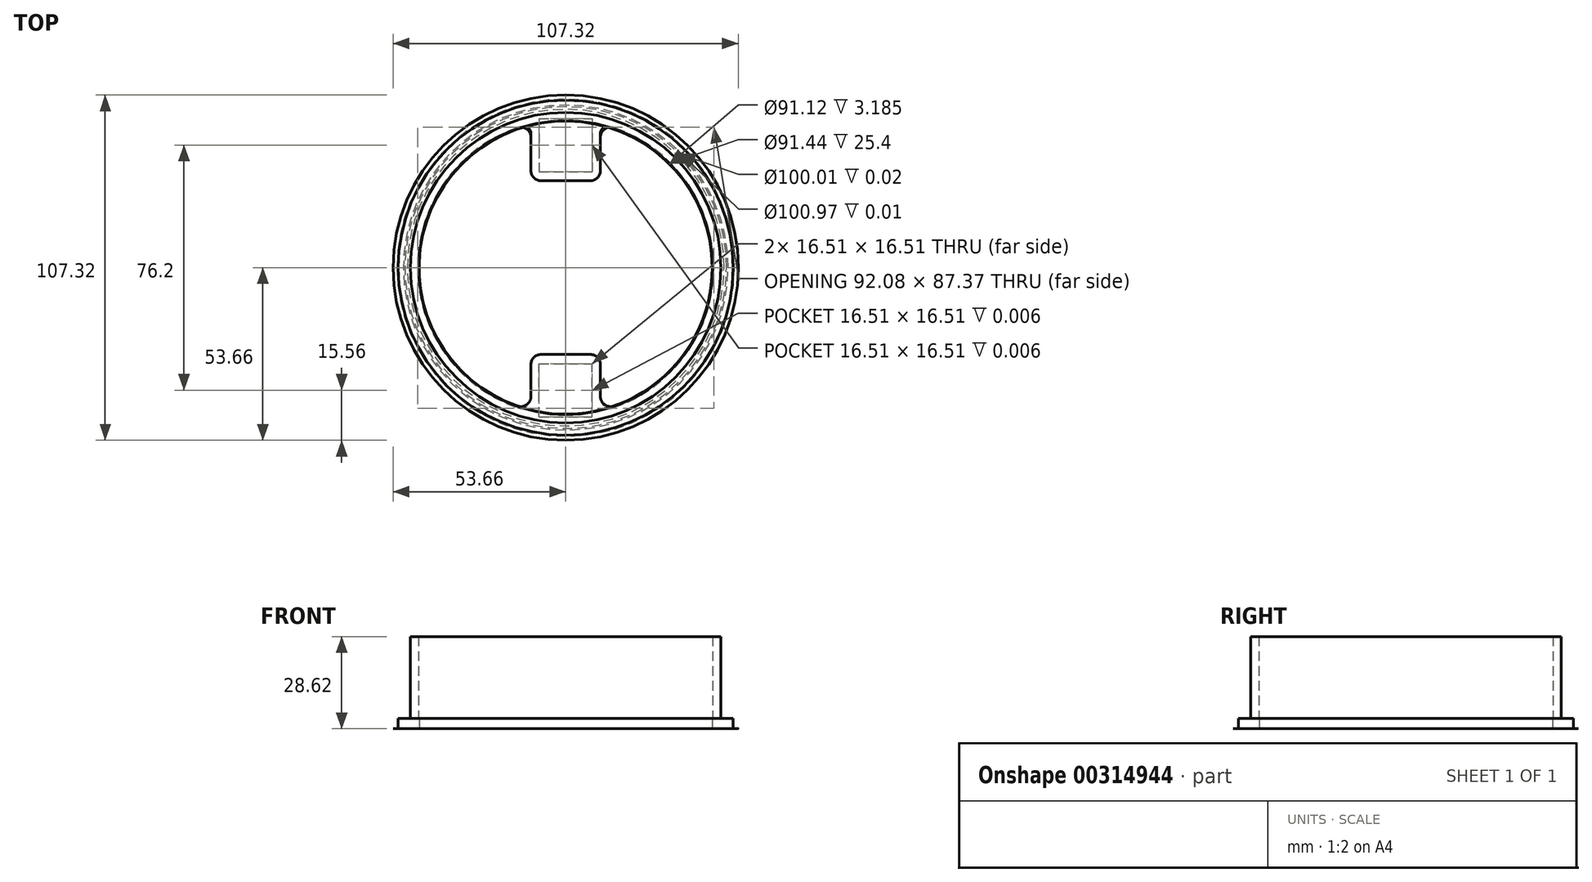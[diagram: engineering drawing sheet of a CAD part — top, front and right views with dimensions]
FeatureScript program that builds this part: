
annotation { "Feature Type Name" : "Feature", "Feature Type Description" : "" }
export const myFeature = defineFeature(function(context is Context, id is Id, definition is map)
    precondition{}
    {
        {
            var Q0;
            Q0=qCreatedBy(makeId("Top.planeOp"),FACE);
            var sketch = newSketch(context, id + "F0", { "sketchPlane" : qUnion([Q0])});
            skCircle(sketch, "E0", {"center": v(0, 0) * mm, "radius": 50 * mm});
            skCircle(sketch, "E1", {"center": v(0, 0) * mm, "radius": 52.39 * mm});
            skSolve(sketch);
        }
        {
            var Q0;
            Q0=qSketchRegion(id+"F0",true);
            extrude(context, id + "F1", {"entities" : qUnion([Q0]), "depth" : 1 / 50.8 * mm});
        }
        {
            var Q0;
            Q0=makeQuery(id+"F1.opExtrude","CAP_FACE",FACE,{"disambiguationData":[OSD([sQuery(id+"F0.wireOp",EDGE,"E0"),sQuery(id+"F0.wireOp",EDGE,"E1")])],"isStart":false});
            var sketch = newSketch(context, id + "F2", { "sketchPlane" : qUnion([Q0])});
            skCircle(sketch, "E2.0", {"center": v(0, 0) * mm, "radius": 52.39 * mm});
            skArc(sketch, "E3.0", {"start": v(-15, 43.52) * mm, "mid": v(-46.04, 0) * mm, "end": v(-15, -43.52) * mm});
            skPoint(sketch, "E4.middle", {"position": v(0, 39.69) * mm});
            skPoint(sketch, "E5.orphan", {"position": v(-12.07, 48.74) * mm});
            skPoint(sketch, "E6.orphan", {"position": v(10.8, 48.25) * mm});
            skLineSegment(sketch, "E7.MirrorCS", {"start": v(-10.8, -40.52) * mm, "end": v(-10.8, -30.16) * mm});
            skArc(sketch, "E8.trimOffspring", {"start": v(15, -43.52) * mm, "mid": v(46.04, 0) * mm, "end": v(15, 43.52) * mm});
            skPoint(sketch, "E9.visualSharp", {"position": v(-10.8, -44.75) * mm});
            skArc(sketch, "E9.filletArc", {"start": v(-15, -43.52) * mm, "mid": v(-12.13, -43.1) * mm, "end": v(-10.8, -40.52) * mm});
            skPoint(sketch, "E10.visualSharp", {"position": v(-10.8, -31.13) * mm});
            skPoint(sketch, "E11.visualSharp", {"position": v(12.06, -32.23) * mm});
            skPoint(sketch, "E12.visualSharp", {"position": v(19.77, -41.58) * mm});
            skPoint(sketch, "E13.visualSharp", {"position": v(-10.8, 31.13) * mm});
            skPoint(sketch, "E14.visualSharp", {"position": v(-10.8, 44.75) * mm});
            skPoint(sketch, "E15.visualSharp", {"position": v(19.77, 41.58) * mm});
            skLineSegment(sketch, "E16", {"start": v(7.62, -26.99) * mm, "end": v(-7.62, -26.99) * mm});
            skPoint(sketch, "E17.visualSharp", {"position": v(7.88, -26.99) * mm});
            skPoint(sketch, "E18.visualSharp", {"position": v(-10.8, -26.99) * mm});
            skArc(sketch, "E18.filletArc", {"start": v(-7.62, -26.99) * mm, "mid": v(-9.87, -27.92) * mm, "end": v(-10.8, -30.16) * mm});
            skLineSegment(sketch, "E19.MirrorCS", {"start": v(7.62, 26.99) * mm, "end": v(-7.62, 26.99) * mm});
            skArc(sketch, "E20.MirrorCS", {"start": v(-7.62, 26.99) * mm, "mid": v(-9.87, 27.92) * mm, "end": v(-10.8, 30.16) * mm});
            skLineSegment(sketch, "E21.MirrorCS", {"start": v(-10.8, 40.52) * mm, "end": v(-10.8, 30.16) * mm});
            skLineSegment(sketch, "E22.MirrorCS", {"start": v(10.8, 40.52) * mm, "end": v(10.8, 30.16) * mm});
            skArc(sketch, "E23.MirrorCS", {"start": v(7.62, 26.99) * mm, "mid": v(9.87, 27.92) * mm, "end": v(10.8, 30.16) * mm});
            skArc(sketch, "E24.MirrorCS", {"start": v(7.62, -26.99) * mm, "mid": v(9.87, -27.92) * mm, "end": v(10.8, -30.16) * mm});
            skLineSegment(sketch, "E25.MirrorCS", {"start": v(10.8, -40.52) * mm, "end": v(10.8, -30.16) * mm});
            skArc(sketch, "E26.MirrorCS", {"start": v(15, -43.52) * mm, "mid": v(12.13, -43.1) * mm, "end": v(10.8, -40.52) * mm});
            skPoint(sketch, "E27.orphan", {"position": v(5.08, 26.99) * mm});
            skPoint(sketch, "E28.orphan", {"position": v(5.08, -26.99) * mm});
            skArc(sketch, "E29.MirrorCS", {"start": v(-15, 43.52) * mm, "mid": v(-12.13, 43.1) * mm, "end": v(-10.8, 40.52) * mm});
            skArc(sketch, "E30.MirrorCS", {"start": v(15, 43.52) * mm, "mid": v(12.13, 43.1) * mm, "end": v(10.8, 40.52) * mm});
            skSolve(sketch);
        }
        {
            var Q0;
            Q0=qSketchRegion(id+"F2",true);
            extrude(context, id + "F3", {"entities" : qUnion([Q0]), "operationType" : NewBodyOperationType.ADD, "depth" : 1 / 101.6 * mm});
        }
        {
            var Q0;
            Q0=makeQuery(id+"F3.opExtrude","CAP_FACE",FACE,{"disambiguationData":[OSD([sQuery(id+"F2.wireOp",EDGE,"E2.0"),sQuery(id+"F2.wireOp",EDGE,"E3.0")])],"isStart":false});
            var sketch = newSketch(context, id + "F4", { "sketchPlane" : qUnion([Q0])});
            skCircle(sketch, "E31", {"center": v(0, 0) * mm, "radius": 50.48 * mm});
            skCircle(sketch, "E32.0", {"center": v(0, 0) * mm, "radius": 53.66 * mm});
            skSolve(sketch);
        }
        {
            var Q0;
            Q0=qSketchRegion(id+"F4",true);
            extrude(context, id + "F5", {"entities" : qUnion([Q0]), "operationType" : NewBodyOperationType.ADD, "depth" : 1 / 101.6 * mm});
        }
        {
            var Q0;
            Q0=makeQuery(id+"F3.opExtrude","CAP_FACE",FACE,{"disambiguationData":[OSD([sQuery(id+"F2.wireOp",EDGE,"E2.0"),sQuery(id+"F2.wireOp",EDGE,"E3.0"),sQuery(id+"F2.wireOp",EDGE,"E4.top"),sQuery(id+"F2.wireOp",EDGE,"E4.left"),sQuery(id+"F2.wireOp",EDGE,"E4.right"),sQuery(id+"F2.wireOp",EDGE,"E7.MirrorCS"),sQuery(id+"F2.wireOp",EDGE,"14d7e438-5bb9-4d8e-acd8-ebce0bf1a9fc0.MirrorCS"),sQuery(id+"F2.wireOp",EDGE,"57ccc243-d271-415f-816b-320263d1c3790.MirrorCS"),sQuery(id+"F2.wireOp",EDGE,"E8.trimOffspring"),sQuery(id+"F2.wireOp",EDGE,"E9.filletArc"),sQuery(id+"F2.wireOp",EDGE,"E10.filletArc"),sQuery(id+"F2.wireOp",EDGE,"E11.filletArc"),sQuery(id+"F2.wireOp",EDGE,"E12.filletArc"),sQuery(id+"F2.wireOp",EDGE,"E13.filletArc"),sQuery(id+"F2.wireOp",EDGE,"E14.filletArc"),sQuery(id+"F2.wireOp",EDGE,"E15.filletArc"),sQuery(id+"F2.wireOp",EDGE,"87325a1d-47ca-4d5e-9cd2-0e4b37ab90e0.filletArc")])],"isStart":false});
            var sketch = newSketch(context, id + "F6", { "sketchPlane" : qUnion([Q0])});
            skLineSegment(sketch, "E33.bottom", {"start": v(8.25, 46.35) * mm, "end": v(-8.26, 46.35) * mm});
            skLineSegment(sketch, "E33.top", {"start": v(8.25, 29.84) * mm, "end": v(-8.26, 29.84) * mm});
            skLineSegment(sketch, "E33.left", {"start": v(8.25, 46.35) * mm, "end": v(8.25, 29.84) * mm});
            skLineSegment(sketch, "E33.right", {"start": v(-8.26, 46.35) * mm, "end": v(-8.26, 29.84) * mm});
            skPoint(sketch, "E33.middle", {"position": v(0, 38.1) * mm});
            skLineSegment(sketch, "E34.MirrorCS", {"start": v(-8.26, -46.35) * mm, "end": v(-8.26, -29.84) * mm});
            skLineSegment(sketch, "E35.MirrorCS", {"start": v(8.25, -46.35) * mm, "end": v(8.25, -29.84) * mm});
            skLineSegment(sketch, "E36.MirrorCS", {"start": v(8.25, -29.84) * mm, "end": v(-8.26, -29.84) * mm});
            skLineSegment(sketch, "E37.MirrorCS", {"start": v(8.25, -46.35) * mm, "end": v(-8.26, -46.35) * mm});
            skPoint(sketch, "E38.MirrorP", {"position": v(0, -38.1) * mm});
            skSolve(sketch);
        }
        {
            var Q0;
            Q0=qSketchRegion(id+"F6",true);
            extrude(context, id + "F7", {"entities" : qUnion([Q0]), "operationType" : NewBodyOperationType.REMOVE, "oppositeDirection" : true, "depth" : 1 / 152.4 * mm});
        }
        {
            var Q0;
            Q0=makeQuery(id+"F5.opExtrude","CAP_FACE",FACE,{"disambiguationData":[OSD([sQuery(id+"F4.wireOp",EDGE,"E31"),sQuery(id+"F4.wireOp",EDGE,"E32.0")])],"isStart":false});
            var sketch = newSketch(context, id + "F8", { "sketchPlane" : qUnion([Q0])});
            skCircle(sketch, "E39.0", {"center": v(0, 0) * mm, "radius": 49.21 * mm});
            skArc(sketch, "E40.0", {"start": v(-10.8, 41.77) * mm, "mid": v(-11.57, 43.3) * mm, "end": v(-13.25, 43.6) * mm});
            skLineSegment(sketch, "E40.7", {"start": v(-10.8, -40.02) * mm, "end": v(-10.8, -30.16) * mm});
            skLineSegment(sketch, "E40.10", {"start": v(10.8, -40.02) * mm, "end": v(10.8, -30.16) * mm});
            skArc(sketch, "E40.13", {"start": v(13.25, 43.6) * mm, "mid": v(11.57, 43.3) * mm, "end": v(10.8, 41.77) * mm});
            skLineSegment(sketch, "E41", {"start": v(-7.62, -26.99) * mm, "end": v(7.62, -26.99) * mm});
            skLineSegment(sketch, "E42.MirrorCS", {"start": v(-7.62, 26.99) * mm, "end": v(7.62, 26.99) * mm});
            skLineSegment(sketch, "E43.MirrorCS", {"start": v(-10.8, 41.77) * mm, "end": v(-10.8, 30.16) * mm});
            skLineSegment(sketch, "E44.MirrorCS", {"start": v(10.8, 41.77) * mm, "end": v(10.8, 30.16) * mm});
            skPoint(sketch, "E45.visualSharp", {"position": v(-10.8, -26.99) * mm});
            skArc(sketch, "E45.filletArc", {"start": v(-7.62, -26.99) * mm, "mid": v(-9.87, -27.92) * mm, "end": v(-10.8, -30.16) * mm});
            skPoint(sketch, "E46.visualSharp", {"position": v(10.8, -26.99) * mm});
            skArc(sketch, "E46.filletArc", {"start": v(10.8, -30.16) * mm, "mid": v(9.87, -27.92) * mm, "end": v(7.62, -26.99) * mm});
            skPoint(sketch, "E47.visualSharp", {"position": v(10.8, 26.99) * mm});
            skArc(sketch, "E47.filletArc", {"start": v(7.62, 26.99) * mm, "mid": v(9.87, 27.92) * mm, "end": v(10.8, 30.16) * mm});
            skPoint(sketch, "E48.visualSharp", {"position": v(-10.8, 26.99) * mm});
            skArc(sketch, "E48.filletArc", {"start": v(-10.8, 30.16) * mm, "mid": v(-9.87, 27.92) * mm, "end": v(-7.62, 26.99) * mm});
            skArc(sketch, "E49", {"start": v(-13.25, 43.6) * mm, "mid": v(-45.55, 0.93) * mm, "end": v(-15.02, -43.02) * mm});
            skPoint(sketch, "E50.orphan", {"position": v(-10.8, -41.36) * mm});
            skPoint(sketch, "E51.orphan", {"position": v(10.8, -41.77) * mm});
            skArc(sketch, "E52.trimOffspring", {"start": v(15.02, -43.02) * mm, "mid": v(45.55, 0.93) * mm, "end": v(13.25, 43.6) * mm});
            skPoint(sketch, "E53.visualSharp", {"position": v(-10.8, -44.26) * mm});
            skArc(sketch, "E53.filletArc", {"start": v(-15.02, -43.02) * mm, "mid": v(-12.13, -42.6) * mm, "end": v(-10.8, -40.02) * mm});
            skPoint(sketch, "E54.visualSharp", {"position": v(10.8, -44.26) * mm});
            skArc(sketch, "E54.filletArc", {"start": v(10.8, -40.02) * mm, "mid": v(12.13, -42.6) * mm, "end": v(15.02, -43.02) * mm});
            skPoint(sketch, "E55.orphan", {"position": v(-10.8, 41.36) * mm});
            skSolve(sketch);
        }
        {
            var Q0;
            Q0=qSketchRegion(id+"F8",true);
            extrude(context, id + "F9", {"entities" : qUnion([Q0]), "operationType" : NewBodyOperationType.ADD, "depth" : 1 / 101.6 * mm});
        }
        {
            var Q0;
            Q0=makeQuery(id+"F9.opExtrude","CAP_FACE",FACE,{"disambiguationData":[OSD([sQuery(id+"F8.wireOp",EDGE,"E39.0"),sQuery(id+"F8.wireOp",EDGE,"E40.0"),sQuery(id+"F8.wireOp",EDGE,"E40.1"),sQuery(id+"F8.wireOp",EDGE,"E40.2"),sQuery(id+"F8.wireOp",EDGE,"E40.3"),sQuery(id+"F8.wireOp",EDGE,"E40.4"),sQuery(id+"F8.wireOp",EDGE,"E40.5"),sQuery(id+"F8.wireOp",EDGE,"E40.6"),sQuery(id+"F8.wireOp",EDGE,"E40.7"),sQuery(id+"F8.wireOp",EDGE,"E40.8"),sQuery(id+"F8.wireOp",EDGE,"E40.9"),sQuery(id+"F8.wireOp",EDGE,"E40.10"),sQuery(id+"F8.wireOp",EDGE,"E40.11"),sQuery(id+"F8.wireOp",EDGE,"E40.12"),sQuery(id+"F8.wireOp",EDGE,"E40.13"),sQuery(id+"F8.wireOp",EDGE,"E40.14"),sQuery(id+"F8.wireOp",EDGE,"E40.15")])],"isStart":false});
            var sketch = newSketch(context, id + "F10", { "sketchPlane" : qUnion([Q0])});
            skCircle(sketch, "E56", {"center": v(0, 0) * mm, "radius": 52.07 * mm});
            skCircle(sketch, "E57", {"center": v(0, 0) * mm, "radius": 45.56 * mm});
            skSolve(sketch);
        }
        {
            var Q0;
            Q0=qSketchRegion(id+"F10",true);
            extrude(context, id + "F11", {"entities" : qUnion([Q0]), "operationType" : NewBodyOperationType.ADD, "depth" : 3.17 * mm});
        }
        {
            var Q0;
            Q0=makeQuery(id+"F11.opExtrude","CAP_FACE",FACE,{"disambiguationData":[OSD([sQuery(id+"F10.wireOp",EDGE,"E56"),sQuery(id+"F10.wireOp",EDGE,"E57")])],"isStart":false});
            var sketch = newSketch(context, id + "F12", { "sketchPlane" : qUnion([Q0])});
            skCircle(sketch, "E58", {"center": v(0, 0) * mm, "radius": 48.26 * mm});
            skCircle(sketch, "E59", {"center": v(0, 0) * mm, "radius": 45.72 * mm});
            skSolve(sketch);
        }
        {
            var Q0;
            Q0=qSketchRegion(id+"F12",true);
            extrude(context, id + "F13", {"entities" : qUnion([Q0]), "operationType" : NewBodyOperationType.ADD, "depth" : 25.4 * mm});
        }
        {
            var Q0;
            Q0=makeQuery(id+"F9.opExtrude","CAP_FACE",FACE,{"disambiguationData":[OSD([sQuery(id+"F8.wireOp",EDGE,"E39.0"),sQuery(id+"F8.wireOp",EDGE,"E40.0"),sQuery(id+"F8.wireOp",EDGE,"E40.1"),sQuery(id+"F8.wireOp",EDGE,"E40.2"),sQuery(id+"F8.wireOp",EDGE,"E40.3"),sQuery(id+"F8.wireOp",EDGE,"E40.4"),sQuery(id+"F8.wireOp",EDGE,"E40.5"),sQuery(id+"F8.wireOp",EDGE,"E40.6"),sQuery(id+"F8.wireOp",EDGE,"E40.7"),sQuery(id+"F8.wireOp",EDGE,"E40.8"),sQuery(id+"F8.wireOp",EDGE,"E40.9"),sQuery(id+"F8.wireOp",EDGE,"E40.10"),sQuery(id+"F8.wireOp",EDGE,"E40.11"),sQuery(id+"F8.wireOp",EDGE,"E40.12"),sQuery(id+"F8.wireOp",EDGE,"E40.13"),sQuery(id+"F8.wireOp",EDGE,"E40.14"),sQuery(id+"F8.wireOp",EDGE,"E40.15")])],"isStart":true});
            var sketch = newSketch(context, id + "F14", { "sketchPlane" : qUnion([Q0])});
            skLineSegment(sketch, "E60.bottom", {"start": v(-8.26, -46.35) * mm, "end": v(8.26, -46.35) * mm});
            skLineSegment(sketch, "E60.top", {"start": v(-8.26, -29.84) * mm, "end": v(8.26, -29.84) * mm});
            skLineSegment(sketch, "E60.left", {"start": v(-8.26, -46.35) * mm, "end": v(-8.26, -29.84) * mm});
            skLineSegment(sketch, "E60.right", {"start": v(8.26, -46.35) * mm, "end": v(8.26, -29.84) * mm});
            skPoint(sketch, "E60.middle", {"position": v(0, -38.1) * mm});
            skPoint(sketch, "E60.middle.positionSnap0", {"position": v(10.8, -38.1) * mm});
            skPoint(sketch, "E60.centerSnap0", {"position": v(10.8, -38.1) * mm});
            skPoint(sketch, "E61.MirrorP", {"position": v(10.8, 38.1) * mm});
            skLineSegment(sketch, "E62.MirrorCS", {"start": v(8.25, 46.35) * mm, "end": v(8.25, 29.84) * mm});
            skLineSegment(sketch, "E63.MirrorCS", {"start": v(-8.26, 46.35) * mm, "end": v(-8.26, 29.84) * mm});
            skLineSegment(sketch, "E64.MirrorCS", {"start": v(-8.26, 29.84) * mm, "end": v(8.26, 29.84) * mm});
            skLineSegment(sketch, "E65.MirrorCS", {"start": v(-8.26, 46.35) * mm, "end": v(8.26, 46.35) * mm});
            skPoint(sketch, "E66.MirrorP", {"position": v(0, 38.1) * mm});
            skSolve(sketch);
        }
        {
            var Q0;
            Q0=qSketchRegion(id+"F14",true);
            extrude(context, id + "F15", {"entities" : qUnion([Q0]), "operationType" : NewBodyOperationType.REMOVE, "oppositeDirection" : true, "depth" : 1 / 152.4 * mm});
        }
    });
